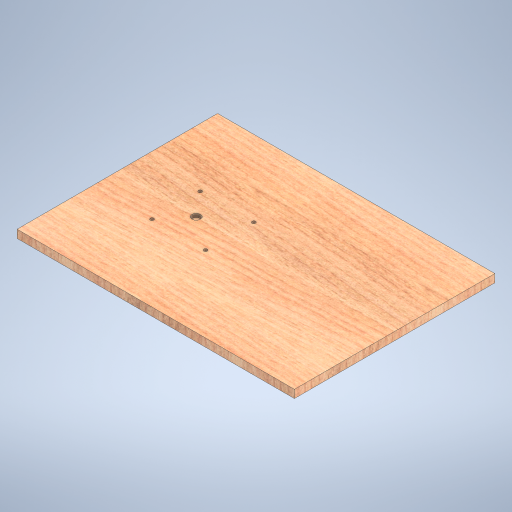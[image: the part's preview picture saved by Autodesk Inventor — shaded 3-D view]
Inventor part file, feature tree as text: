
AUTODESK INVENTOR PART (.ipt)
format: ipt  version: 2024.2 (Build 282272000, 272)  size: 413,184 bytes
history: native  units: mm
features: sketch x4, reference x4, other x4, extrude x3, hole x1
ambient origin geometry x8: Origin, YZ Plane, XZ Plane, XY Plane, X Axis, Y Axis, Z Axis, Center Point
bodies: Body1 (feature_tree)
feature tree (16):
  extrude  "Extrusion4"  Depth=300.0mm
  hole  "Hole3"  [1 undecoded]
  extrude  "Extrusion5"  Depth=5.29mm
  extrude  "Extrusion6"  Depth=10.0mm TaperAngle=0.0deg
  sketch  "Sketch7"  dims[d32=350.0mm d33=300.0mm]
  sketch  "Sketch8"  dims[d34=52.95mm d35=12.0mm d36=0.0mm]
  reference  "Reference2"
  reference  "Reference3"
  reference  "Reference4"
  reference  "Reference5"
  sketch  "Sketch9"  dims[d37=14.0mm]
  sketch  "Sketch10"  dims[d38=5.2mm d39=6.0mm d40=12.0mm d41=3.0mm d42=90.0deg d43=8.0mm d44=20.594885mm d45=65.0mm d46=10.0mm d47=0.0mm d48=117.95mm d49=12.8mm d50=5.29mm d51=0.0mm]
  other  "0_Entire_Assembly.iam"
  other  "2_Arm:1"
  other  "Aluminum_Profile_4040_100.14mm_bottom:1"
  other  "Aluminum_Profile_4040_100.14mm_top:1"
note: 1 required parameter value undecoded (feature->parameter linkage not recoverable at this tier; creation-order binding heuristic only, values carry confidence <= 0.55)
